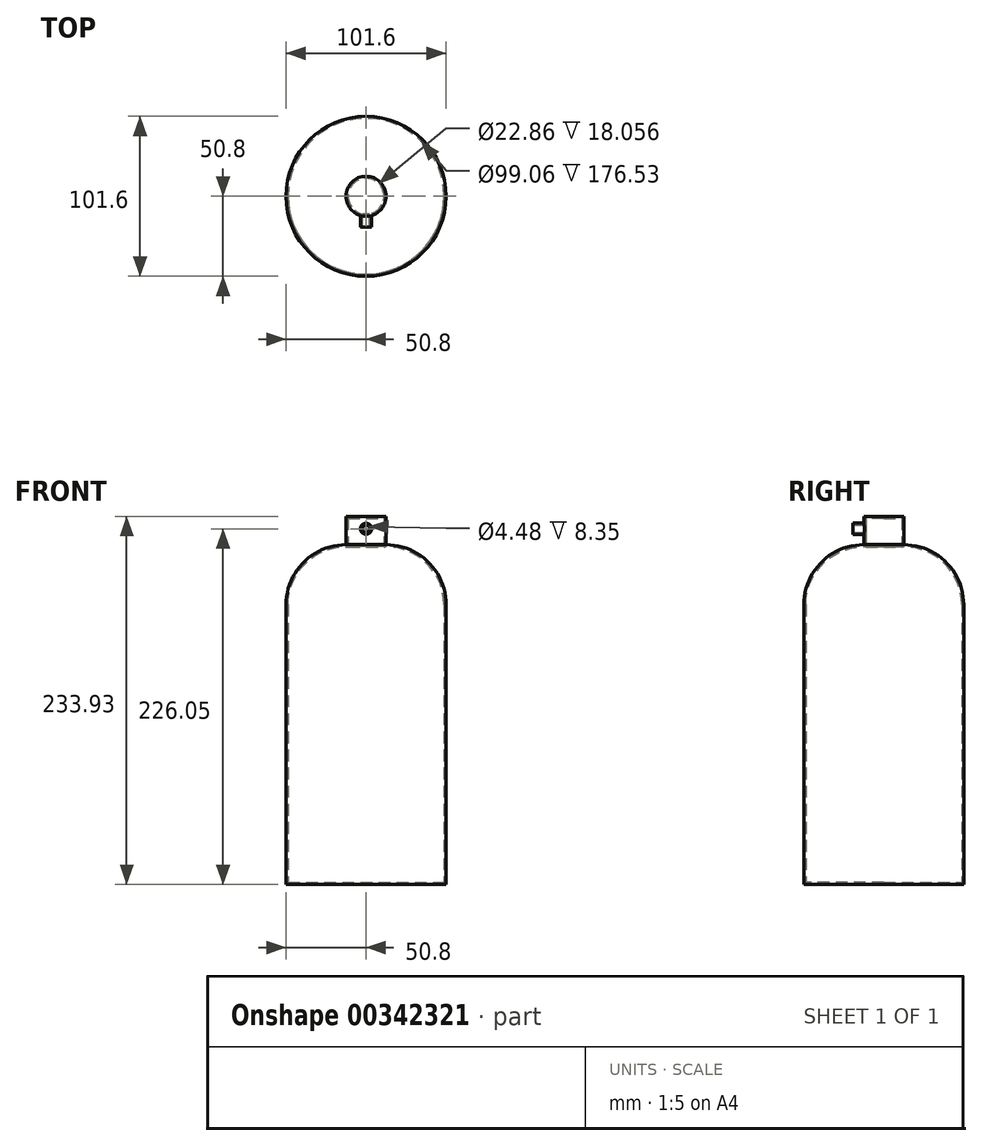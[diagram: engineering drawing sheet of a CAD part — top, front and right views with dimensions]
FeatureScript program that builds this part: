
annotation { "Feature Type Name" : "Feature", "Feature Type Description" : "" }
export const myFeature = defineFeature(function(context is Context, id is Id, definition is map)
    precondition{}
    {
        {
            var Q0;
            Q0=qCreatedBy(makeId("Top.planeOp"),FACE);
            var sketch = newSketch(context, id + "F0", { "sketchPlane" : qUnion([Q0])});
            skCircle(sketch, "E0", {"center": v(0, 0) * mm, "radius": 50.8 * mm});
            skSolve(sketch);
        }
        {
            var Q0;
            Q0=makeQuery(id+"F0.imprint","IMPRINT",FACE,{"disambiguationData":[TD([[makeQuery(id+"F0.imprint","IMPRINT",EDGE,{"derivedFrom":sQuery(id+"F0.wireOp",EDGE,"E0")}),1.0]])]});
            extrude(context, id + "F1", {"entities" : qUnion([Q0]), "depth" : 215.9 * mm});
        }
        {
            var Q0;
            Q0=makeQuery(id+"F1.opExtrude","CAP_EDGE",EDGE,{"disambiguationData":[OSD([sQuery(id+"F0.wireOp",EDGE,"E0")])],"isStart":false});
            fillet(context, id + "F2", {"entities" : qUnion([Q0]), "radius" : 38.1 * mm, "tangentPropagation" : true, "allowEdgeOverflow" : false});
        }
        {
            var Q0;
            Q0=makeQuery(id+"F1.opExtrude","CAP_FACE",FACE,{"disambiguationData":[OSD([sQuery(id+"F0.wireOp",EDGE,"E0")])],"isStart":false});
            extrude(context, id + "F3", {"entities" : qUnion([Q0]), "operationType" : NewBodyOperationType.ADD, "depth" : 18.03 * mm});
        }
        {
            var Q0;
            Q0=qCreatedBy(makeId("Front.planeOp"),FACE);
            var sketch = newSketch(context, id + "F4", { "sketchPlane" : qUnion([Q0])});
            skCircle(sketch, "E1", {"center": v(0, 226.05) * mm, "radius": 3.51 * mm});
            skSolve(sketch);
        }
        {
            var Q0;
            Q0 = qSketchRegion(id + "F4", true);
            extrude(context, id + "F5", {"entities" : qUnion([Q0]), "operationType" : NewBodyOperationType.ADD, "depth" : 19.56 * mm});
        }
        {
            var Q0;
            Q0=makeQuery(id+"F5.opExtrude","CAP_FACE",FACE,{"disambiguationData":[OSD([sQuery(id+"F4.wireOp",EDGE,"E1")])],"isStart":false});
            shell(context, id + "F6", {"entities" : qUnion([Q0]), "thickness" : 1.27 * mm});
        }
    });
